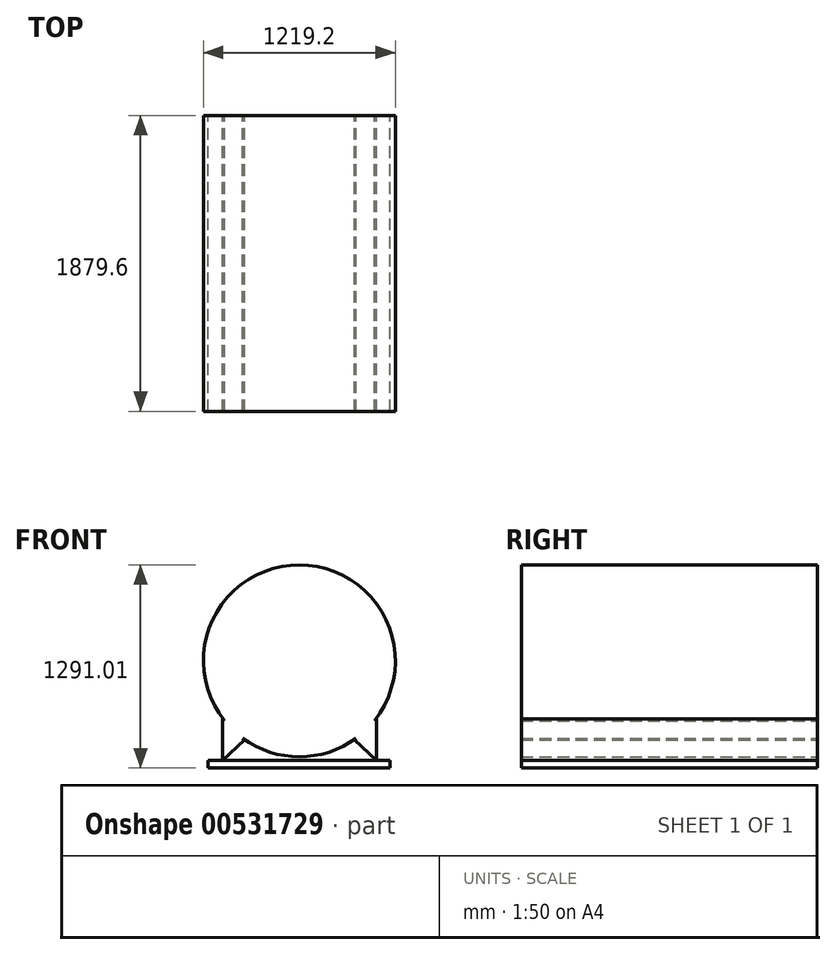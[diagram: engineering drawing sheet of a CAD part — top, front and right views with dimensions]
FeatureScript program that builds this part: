
annotation { "Feature Type Name" : "Feature", "Feature Type Description" : "" }
export const myFeature = defineFeature(function(context is Context, id is Id, definition is map)
    precondition{}
    {
        {
            var Q0;
            Q0=qCreatedBy(makeId("Front.planeOp"),FACE);
            var sketch = newSketch(context, id + "F0", { "sketchPlane" : qUnion([Q0])});
            skCircle(sketch, "E0", {"center": v(0, 0) * mm, "radius": 609.6 * mm});
            skSolve(sketch);
        }
        {
            var Q0;
            Q0=makeQuery(id+"F0.imprint","IMPRINT",FACE,{"disambiguationData":[TD([[makeQuery(id+"F0.imprint","IMPRINT",EDGE,{"derivedFrom":sQuery(id+"F0.wireOp",EDGE,"E0")}),1.0]])]});
            extrude(context, id + "F1", {"entities" : qUnion([Q0]), "depth" : 1879.6 * mm, "offsetDistance" : 25.4 * mm});
        }
        {
            var Q0;
            Q0=qCreatedBy(makeId("Front.planeOp"),FACE);
            var sketch = newSketch(context, id + "F2", { "sketchPlane" : qUnion([Q0])});
            skLineSegment(sketch, "E1", {"start": v(-489.2, -368.11) * mm, "end": v(-489.2, -631.02) * mm});
            skLineSegment(sketch, "E2", {"start": v(-489.2, -631.02) * mm, "end": v(-348.99, -502.49) * mm});
            skLineSegment(sketch, "E3", {"start": v(-348.99, -502.49) * mm, "end": v(-489.2, -368.11) * mm});
            skLineSegment(sketch, "E4.MirrorCS", {"start": v(489.2, -368.11) * mm, "end": v(489.2, -631.02) * mm});
            skLineSegment(sketch, "E5.MirrorCS", {"start": v(348.99, -502.49) * mm, "end": v(489.2, -368.11) * mm});
            skLineSegment(sketch, "E6.MirrorCS", {"start": v(489.2, -631.02) * mm, "end": v(348.99, -502.49) * mm});
            skLineSegment(sketch, "E7", {"start": v(-489.2, -631.02) * mm, "end": v(489.2, -631.02) * mm});
            skLineSegment(sketch, "E8", {"start": v(575.42, -631.02) * mm, "end": v(575.42, -681.41) * mm});
            skLineSegment(sketch, "E9", {"start": v(575.42, -681.41) * mm, "end": v(-580.69, -681.41) * mm});
            skLineSegment(sketch, "E10", {"start": v(-580.69, -681.41) * mm, "end": v(-580.69, -631.02) * mm});
            skLineSegment(sketch, "E11", {"start": v(-580.69, -631.02) * mm, "end": v(-489.2, -631.02) * mm});
            skLineSegment(sketch, "E12", {"start": v(489.2, -631.02) * mm, "end": v(575.42, -631.02) * mm});
            skSolve(sketch);
        }
        {
            var Q0;
            Q0 = qSketchRegion(id + "F2", true);
            extrude(context, id + "F3", {"entities" : qUnion([Q0]), "operationType" : NewBodyOperationType.ADD, "depth" : 1879.6 * mm, "offsetDistance" : 25.4 * mm});
        }
    });
